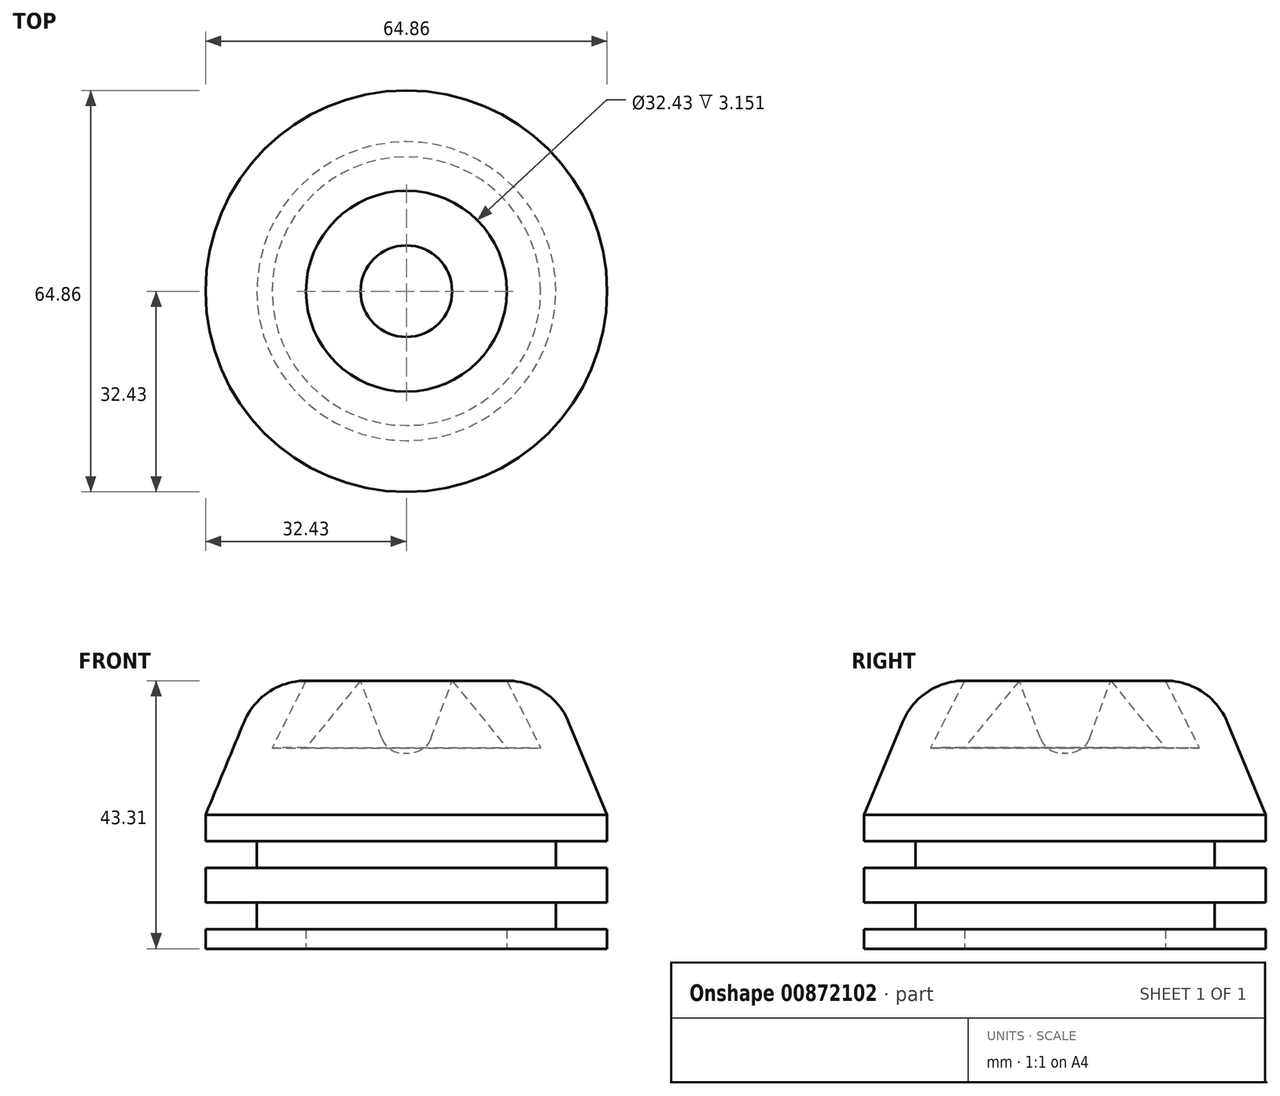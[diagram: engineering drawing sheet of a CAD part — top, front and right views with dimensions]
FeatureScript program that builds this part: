
annotation { "Feature Type Name" : "Feature", "Feature Type Description" : "" }
export const myFeature = defineFeature(function(context is Context, id is Id, definition is map)
    precondition{}
    {
        {
            var Q0;
            Q0=qCreatedBy(makeId("Right.planeOp"),FACE);
            var sketch = newSketch(context, id + "F0", { "sketchPlane" : qUnion([Q0])});
            skLineSegment(sketch, "E0.bottom", {"start": v(0, 0) * mm, "end": v(32.43, 0) * mm});
            skLineSegment(sketch, "E0.top", {"start": v(0, 43.31) * mm, "end": v(32.43, 43.31) * mm});
            skLineSegment(sketch, "E0.left", {"start": v(0, 0) * mm, "end": v(0, 43.31) * mm});
            skLineSegment(sketch, "E0.right", {"start": v(32.43, 0) * mm, "end": v(32.43, 43.31) * mm});
            skLineSegment(sketch, "E1", {"start": v(16.22, 0) * mm, "end": v(16.22, 43.31) * mm});
            skLineSegment(sketch, "E2", {"start": v(0, 21.66) * mm, "end": v(32.43, 21.66) * mm});
            skArc(sketch, "E3", {"start": v(16.22, 21.66) * mm, "mid": v(27.04, 32.48) * mm, "end": v(16.22, 43.31) * mm});
            skLineSegment(sketch, "E4", {"start": v(32.43, 21.66) * mm, "end": v(26.22, 36.63) * mm});
            skLineSegment(sketch, "E5", {"start": v(26.22, 36.63) * mm, "end": v(29.33, 29.15) * mm});
            skLineSegment(sketch, "E6", {"start": v(7.4, 43.31) * mm, "end": v(3.97, 34.02) * mm});
            skArc(sketch, "E7", {"start": v(3.97, 34.02) * mm, "mid": v(3.39, 37.63) * mm, "end": v(0, 39.01) * mm});
            skLineSegment(sketch, "E8", {"start": v(7.4, 43.31) * mm, "end": v(16.22, 32.48) * mm});
            skLineSegment(sketch, "E9", {"start": v(16.22, 43.31) * mm, "end": v(21.7, 32.45) * mm});
            skLineSegment(sketch, "E10", {"start": v(21.7, 32.45) * mm, "end": v(16.22, 32.48) * mm});
            skLineSegment(sketch, "E11", {"start": v(24.15, 21.66) * mm, "end": v(24.15, 0) * mm});
            skLineSegment(sketch, "E12.top", {"start": v(0, 17.36) * mm, "end": v(32.43, 17.36) * mm});
            skLineSegment(sketch, "E12.left", {"start": v(0, 21.66) * mm, "end": v(0, 17.36) * mm});
            skLineSegment(sketch, "E12.right", {"start": v(32.43, 21.66) * mm, "end": v(32.43, 17.36) * mm});
            skLineSegment(sketch, "E13.top", {"start": v(0, 13.05) * mm, "end": v(32.43, 13.05) * mm});
            skLineSegment(sketch, "E13.left", {"start": v(0, 17.36) * mm, "end": v(0, 13.05) * mm});
            skLineSegment(sketch, "E13.right", {"start": v(32.43, 17.36) * mm, "end": v(32.43, 13.05) * mm});
            skLineSegment(sketch, "E14.top", {"start": v(0, 7.46) * mm, "end": v(32.43, 7.46) * mm});
            skLineSegment(sketch, "E14.left", {"start": v(0, 13.05) * mm, "end": v(0, 7.46) * mm});
            skLineSegment(sketch, "E14.right", {"start": v(32.43, 13.05) * mm, "end": v(32.43, 7.46) * mm});
            skLineSegment(sketch, "E15.top", {"start": v(0, 3.15) * mm, "end": v(32.43, 3.15) * mm});
            skLineSegment(sketch, "E15.left", {"start": v(0, 7.46) * mm, "end": v(0, 3.15) * mm});
            skLineSegment(sketch, "E15.right", {"start": v(32.43, 7.46) * mm, "end": v(32.43, 3.15) * mm});
            skSolve(sketch);
        }
        {
            var Q0;
            Q0=makeQuery(id+"F0.imprint","IMPRINT",FACE,{"disambiguationData":[TD([[makeQuery(id+"F0.imprint","IMPRINT",EDGE,{"derivedFrom":sQuery(id+"F0.wireOp",EDGE,"E6")}),1.0]])]});
            var Q1;
            {var subQ0=sQuery(id+"F0.wireOp",EDGE,"E9");Q1=makeQuery(id+"F0.imprint","IMPRINT",FACE,{"disambiguationData":[TD([[makeQuery(id+"F0.imprint","IMPRINT",EDGE,{"derivedFrom":subQ0}),1.0]])]});}
            var Q2;
            {var subQ0=sQuery(id+"F0.wireOp",EDGE,"E4");var subQ3=makeQuery(id+"F0.imprint","IMPRINT",VERTEX,{"derivedFrom":subQ0});Q2=makeQuery(id+"F0.imprint","IMPRINT",FACE,{"disambiguationData":[TD([[makeQuery(id+"F0.imprint","IMPRINT",EDGE,{"disambiguationData":[TD([[subQ3,-1.0]])],"derivedFrom":subQ0}),1.0]])]});}
            var Q3;
            {var subQ0=sQuery(id+"F0.wireOp",EDGE,"E2");var subQ5=sQuery(id+"F0.wireOp",EDGE,"E11");var subQ6=makeQuery(id+"F0.imprint","INTERSECT",VERTEX,{"derivedFrom":[subQ0,subQ5]});Q3=makeQuery(id+"F0.imprint","IMPRINT",FACE,{"disambiguationData":[TD([[makeQuery(id+"F0.imprint","IMPRINT",EDGE,{"disambiguationData":[TD([[subQ6,-1.0]])],"derivedFrom":subQ5}),1.0]])]});}
            var Q4;
            {var subQ0=sQuery(id+"F0.wireOp",EDGE,"E13.top");var subQ1=sQuery(id+"F0.wireOp",EDGE,"E0.right");var subQ2=makeQuery(id+"F0.imprint","INTERSECT",VERTEX,{"derivedFrom":[subQ1,subQ0]});Q4=makeQuery(id+"F0.imprint","IMPRINT",FACE,{"disambiguationData":[TD([[makeQuery(id+"F0.imprint","IMPRINT",EDGE,{"disambiguationData":[TD([[subQ2,1.0]])],"derivedFrom":subQ1}),1.0]])]});}
            var Q5;
            {var subQ0=sQuery(id+"F0.wireOp",EDGE,"E11");var subQ1=sQuery(id+"F0.wireOp",EDGE,"E0.bottom");var subQ2=makeQuery(id+"F0.imprint","INTERSECT",VERTEX,{"derivedFrom":[subQ1,subQ0]});Q5=makeQuery(id+"F0.imprint","IMPRINT",FACE,{"disambiguationData":[TD([[makeQuery(id+"F0.imprint","IMPRINT",EDGE,{"disambiguationData":[TD([[subQ2,-1.0]])],"derivedFrom":subQ1}),1.0]])]});}
            var Q6;
            {var subQ0=sQuery(id+"F0.wireOp",EDGE,"E2");var subQ5=sQuery(id+"F0.wireOp",EDGE,"E11");var subQ6=makeQuery(id+"F0.imprint","INTERSECT",VERTEX,{"derivedFrom":[subQ0,subQ5]});Q6=makeQuery(id+"F0.imprint","IMPRINT",FACE,{"disambiguationData":[TD([[makeQuery(id+"F0.imprint","IMPRINT",EDGE,{"disambiguationData":[TD([[subQ6,-1.0]])],"derivedFrom":subQ5}),-1.0]])]});}
            var Q7;
            {var subQ0=sQuery(id+"F0.wireOp",EDGE,"E13.top");var subQ1=sQuery(id+"F0.wireOp",EDGE,"E1");var subQ2=makeQuery(id+"F0.imprint","INTERSECT",VERTEX,{"derivedFrom":[subQ1,subQ0]});Q7=makeQuery(id+"F0.imprint","IMPRINT",FACE,{"disambiguationData":[TD([[makeQuery(id+"F0.imprint","IMPRINT",EDGE,{"disambiguationData":[TD([[subQ2,-1.0]])],"derivedFrom":subQ1}),-1.0]])]});}
            var Q8;
            {var subQ0=sQuery(id+"F0.wireOp",EDGE,"E13.top");var subQ1=sQuery(id+"F0.wireOp",EDGE,"E1");var subQ2=makeQuery(id+"F0.imprint","INTERSECT",VERTEX,{"derivedFrom":[subQ1,subQ0]});Q8=makeQuery(id+"F0.imprint","IMPRINT",FACE,{"disambiguationData":[TD([[makeQuery(id+"F0.imprint","IMPRINT",EDGE,{"disambiguationData":[TD([[subQ2,1.0]])],"derivedFrom":subQ1}),-1.0]])]});}
            var Q9;
            {var subQ0=sQuery(id+"F0.wireOp",EDGE,"E15.top");var subQ1=sQuery(id+"F0.wireOp",EDGE,"E1");var subQ2=makeQuery(id+"F0.imprint","INTERSECT",VERTEX,{"derivedFrom":[subQ1,subQ0]});Q9=makeQuery(id+"F0.imprint","IMPRINT",FACE,{"disambiguationData":[TD([[makeQuery(id+"F0.imprint","IMPRINT",EDGE,{"disambiguationData":[TD([[subQ2,-1.0]])],"derivedFrom":subQ1}),-1.0]])]});}
            var Q10;
            {var subQ0=sQuery(id+"F0.wireOp",EDGE,"E11");var subQ1=sQuery(id+"F0.wireOp",EDGE,"E0.bottom");var subQ2=makeQuery(id+"F0.imprint","INTERSECT",VERTEX,{"derivedFrom":[subQ1,subQ0]});Q10=makeQuery(id+"F0.imprint","IMPRINT",FACE,{"disambiguationData":[TD([[makeQuery(id+"F0.imprint","IMPRINT",EDGE,{"disambiguationData":[TD([[subQ2,1.0]])],"derivedFrom":subQ1}),1.0]])]});}
            var Q11;
            {var subQ0=sQuery(id+"F0.wireOp",EDGE,"E15.top");var subQ1=sQuery(id+"F0.wireOp",EDGE,"E0.left");var subQ2=makeQuery(id+"F0.imprint","INTERSECT",VERTEX,{"derivedFrom":[subQ1,subQ0]});Q11=makeQuery(id+"F0.imprint","IMPRINT",FACE,{"disambiguationData":[TD([[makeQuery(id+"F0.imprint","IMPRINT",EDGE,{"disambiguationData":[TD([[subQ2,-1.0]])],"derivedFrom":subQ1}),-1.0]])]});}
            var Q12;
            {var subQ0=sQuery(id+"F0.wireOp",EDGE,"E13.top");var subQ1=sQuery(id+"F0.wireOp",EDGE,"E0.left");var subQ2=makeQuery(id+"F0.imprint","INTERSECT",VERTEX,{"derivedFrom":[subQ1,subQ0]});Q12=makeQuery(id+"F0.imprint","IMPRINT",FACE,{"disambiguationData":[TD([[makeQuery(id+"F0.imprint","IMPRINT",EDGE,{"disambiguationData":[TD([[subQ2,1.0]])],"derivedFrom":subQ1}),-1.0]])]});}
            var Q13;
            {var subQ0=sQuery(id+"F0.wireOp",EDGE,"E12.top");var subQ1=sQuery(id+"F0.wireOp",EDGE,"E0.left");var subQ2=makeQuery(id+"F0.imprint","INTERSECT",VERTEX,{"derivedFrom":[subQ1,subQ0]});Q13=makeQuery(id+"F0.imprint","IMPRINT",FACE,{"disambiguationData":[TD([[makeQuery(id+"F0.imprint","IMPRINT",EDGE,{"disambiguationData":[TD([[subQ2,1.0]])],"derivedFrom":subQ1}),-1.0]])]});}
            var Q14;
            {var subQ0=sQuery(id+"F0.wireOp",EDGE,"E2");var subQ1=sQuery(id+"F0.wireOp",EDGE,"E0.left");var subQ2=makeQuery(id+"F0.imprint","INTERSECT",VERTEX,{"derivedFrom":[subQ1,subQ0]});Q14=makeQuery(id+"F0.imprint","IMPRINT",FACE,{"disambiguationData":[TD([[makeQuery(id+"F0.imprint","IMPRINT",EDGE,{"disambiguationData":[TD([[subQ2,1.0]])],"derivedFrom":subQ1}),-1.0]])]});}
            var Q15;
            Q15=sQuery(id+"F0.wireOp",EDGE,"E0.left");
            revolve(context, id + "F1", {"surfaceOperationType" : NewSurfaceOperationType.NEW, "entities" : qUnion([Q0, Q1, Q2, Q3, Q4, Q5, Q6, Q7, Q8, Q9, Q10, Q11, Q12, Q13, Q14]), "axis" : qUnion([Q15]), "revolveType" : RevolveType.FULL});
        }
    });
